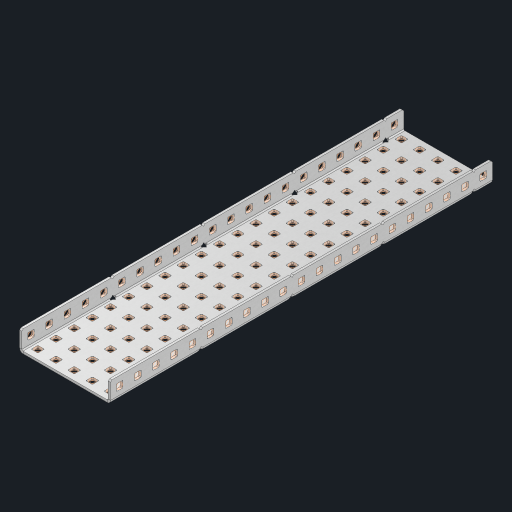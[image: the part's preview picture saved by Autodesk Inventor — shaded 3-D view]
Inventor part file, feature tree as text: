
AUTODESK INVENTOR PART (.ipt)
format: ipt  version: 2023 (Build 270158000, 158)  size: 1,718,272 bytes
history: native  units: in
note: dims shown in document units (in); Inventor stores cm internally (conversion verified against a paired STEP export)
features: other x152, extrude x146, sheet_metal_op x10, sketch x8, mirror x1, pattern_linear x1, chamfer x1
ambient origin geometry x8: Origin, YZ Plane, XZ Plane, XY Plane, X Axis, Y Axis, Z Axis, Center Point
bodies: Solid1 (feature_tree), Body (feature_tree)
feature tree (319):
  other  "Flange Pattern Plane"
  sheet_metal_op  "Flange Pattern"
  sheet_metal_op  "Body Pattern"
  other  "Arc Length"
  mirror  "Notch Mirror"
  pattern_linear  "Notch Pattern"  Spacing1=0.25in  [1 undecoded]
  chamfer  "End Chamfer"
  extrude  "Half Cut"  Depth=0.0625in
  sketch  "Sketch1"  dims[d0=2.5in]
  other  "Plate1"
  sketch  "Sketch2"  dims[d1=10.5in]
  other  "Plate2"
  sheet_metal_op  "Bend1"
  sheet_metal_op  "Corner1"
  sketch  "Sketch3"  dims[d2=0.0625in]
  other  "Flange Pattern Sketch"
  sketch  "Sketch7"  dims[d3=0.0625in]
  other  "Srf1"
  other  "Srf2"
  sketch  "Sketch8"  dims[d4=0.0312in]
  sketch  "Sketch9"  dims[d5=0.125in]
  other  "Srf91"
  sheet_metal_op  "Body Pattern Sketch"
  other  "Srf92"
  sketch  "Sketch13"  dims[d6=0.0625in]
  sketch  "Sketch14"  dims[d7=0.5in d8=90.0deg d9=0.0312in d10=0.25in d11=0.0625in d12=0.0625in d16=0.182in d17=0.02in d18=0.0625in d19=0.0in d20=0.25in d21=0.25in d46=0.172in d47=1.0in d48=0.0in d49=0.182in d50=0.02in d51=0.25in d52=0.25in d53=0.0625in d54=0.0in d55=0.172in d56=1.0in d57=0.0in d60=8.2677in d62=0.5in d63=1.9685in d65=0.5in d85=0.1473in d86=0.1782in d88=0.04in d89=0.0625in d90=0.0in d91=0.04in d92=0.0491in d95=2.5in d96=0.04in d97=0.25in d98=45.0deg d101=0.0in d102=2.497in d131=2.5in d132=8.2677in d134=0.5in d139=0.5in]
  other  "Srf856"
  other  "Srf1310"
  other  "Srf1311"
  other  "Srf1312"
  other  "Srf1376"
  other  "Srf1377"
  other  "Srf1728"
  other  "Srf1755"
  other  "Srf1878"
  other  "Srf1879"
  other  "Srf1880"
  other  "Srf1881"
  other  "Srf1882"
  other  "Srf1883"
  other  "Srf1884"
  other  "Srf1885"
  other  "Srf1886"
  other  "Srf1887"
  other  "Srf1888"
  other  "Srf1889"
  other  "Srf1890"
  other  "Srf1891"
  other  "Srf1892"
  other  "Srf1893"
  other  "Srf1894"
  other  "Srf1895"
  other  "Srf1896"
  other  "Srf1897"
  other  "Srf1898"
  other  "Srf1899"
  other  "Srf1900"
  other  "Srf1901"
  other  "Srf1902"
  other  "Srf1903"
  other  "Srf1904"
  other  "Srf1905"
  other  "Srf1906"
  other  "Srf1942"
  other  "Srf1943"
  other  "Srf1944"
  other  "Srf1945"
  other  "Srf1946"
  other  "Srf1947"
  other  "Srf1948"
  other  "Srf1949"
  other  "Srf1950"
  other  "Srf1951"
  other  "Srf1952"
  other  "Srf1953"
  other  "Srf1954"
  other  "Srf1955"
  other  "Srf1956"
  other  "Srf1957"
  other  "Srf1958"
  other  "Srf1959"
  other  "Srf1960"
  other  "Srf1961"
  other  "Srf1962"
  other  "Srf1963"
  other  "Srf1964"
  other  "Srf1965"
  other  "Srf1966"
  other  "Srf1967"
  other  "Srf1968"
  other  "Srf1969"
  other  "Srf1970"
  other  "Srf2111"
  other  "Srf2112"
  other  "Srf2113"
  other  "Srf2114"
  other  "Srf2115"
  other  "Srf2116"
  other  "Srf2117"
  other  "Srf2146"
  other  "Srf2147"
  other  "Srf2148"
  other  "Srf2149"
  other  "Srf2150"
  other  "Srf2151"
  other  "Srf2152"
  other  "Srf2153"
  other  "Srf2154"
  other  "Srf2155"
  other  "Srf2156"
  other  "Srf2157"
  other  "Srf2158"
  other  "Srf2159"
  other  "Srf2160"
  other  "Srf2161"
  other  "Srf2162"
  other  "Srf2163"
  other  "Srf2164"
  other  "Srf2165"
  other  "Srf2166"
  other  "Srf2167"
  other  "Srf2168"
  other  "Srf2169"
  other  "Srf2170"
  other  "Srf2171"
  other  "Srf2172"
  other  "Srf2173"
  other  "Srf2174"
  other  "Srf2175"
  other  "Srf2176"
  other  "Srf2177"
  other  "Srf2178"
  other  "Srf2179"
  other  "Srf2180"
  other  "Srf2181"
  other  "Srf2182"
  other  "Srf2183"
  other  "Srf2184"
  other  "Srf2185"
  other  "Srf2186"
  other  "Srf2187"
  other  "Srf2188"
  other  "Srf2189"
  other  "Srf2190"
  other  "Srf2191"
  other  "Srf2192"
  other  "Srf2193"
  other  "Srf2194"
  other  "Srf2195"
  other  "Srf2196"
  other  "Srf2197"
  other  "Srf2198"
  other  "Srf2199"
  other  "Srf2200"
  other  "Srf2201"
  other  "Srf2202"
  other  "Srf2203"
  other  "Srf2204"
  other  "Srf2205"
  other  "Srf2206"
  other  "Srf2207"
  other  "Srf2208"
  other  "Srf2209"
  other  "Srf2210"
  other  "Srf2211"
  other  "Srf2212"
  other  "Srf2213"
  other  "Srf2214"
  other  "Srf2215"
  sheet_metal_op  "Flange Stamp"
  sheet_metal_op  "Flange Circle"
  sheet_metal_op  "Body Stamp"
  sheet_metal_op  "Body Circle"
  sheet_metal_op  "Notch"
  extrude  "ExtrusionSrf2"  Depth=0.0625in
  extrude  "ExtrusionSrf92"  Depth=2.5in
  extrude  "ExtrusionSrf856"  Depth=0.02in
  extrude  "ExtrusionSrf1310"  Depth=0.0625in
  extrude  "ExtrusionSrf1311"  TaperAngle=0.0deg  [1 undecoded]
  extrude  "ExtrusionSrf1312"  Depth=0.25in
  extrude  "ExtrusionSrf1376"  Depth=0.25in
  extrude  "ExtrusionSrf1377"  Depth=2.5in
  extrude  "ExtrusionSrf1728"  Depth=2.5in TaperAngle=0.0deg
  extrude  "ExtrusionSrf1755"  Depth=2.5in
  extrude  "ExtrusionSrf1878"  Depth=0.02in
  extrude  "ExtrusionSrf1879"  Depth=0.25in
  extrude  "ExtrusionSrf1880"  Depth=0.25in
  extrude  "ExtrusionSrf1881"  Depth=0.0625in
  extrude  "ExtrusionSrf1882"  TaperAngle=0.0deg  [1 undecoded]
  extrude  "ExtrusionSrf1883"  Depth=2.5in
  extrude  "ExtrusionSrf1884"  Depth=2.5in TaperAngle=0.0deg
  extrude  "ExtrusionSrf1885"  Depth=2.5in
  extrude  "ExtrusionSrf1886"  Depth=2.5in
  extrude  "ExtrusionSrf1887"  Depth=2.5in
  extrude  "ExtrusionSrf1888"  Depth=2.5in
  extrude  "ExtrusionSrf1889"  Depth=2.5in
  extrude  "ExtrusionSrf1890"  Depth=0.0625in
  extrude  "ExtrusionSrf1891"  TaperAngle=0.0deg  [1 undecoded]
  extrude  "ExtrusionSrf1892"  Depth=2.5in
  extrude  "ExtrusionSrf1893"  Depth=2.5in
  extrude  "ExtrusionSrf1894"  Depth=2.5in
  extrude  "ExtrusionSrf1895"  Depth=0.25in TaperAngle=45.0deg
  extrude  "ExtrusionSrf1896"  TaperAngle=0.0deg  [1 undecoded]
  extrude  "ExtrusionSrf1897"  Depth=2.5in
  extrude  "ExtrusionSrf1898"  Depth=2.5in
  extrude  "ExtrusionSrf1899"  Depth=2.5in
  extrude  "ExtrusionSrf1900"  Depth=2.5in
  extrude  "ExtrusionSrf1901"  Depth=2.5in
  extrude  "ExtrusionSrf1902"  [1 undecoded]
  extrude  "ExtrusionSrf1903"  [1 undecoded]
  extrude  "ExtrusionSrf1904"  [1 undecoded]
  extrude  "ExtrusionSrf1905"  [1 undecoded]
  extrude  "ExtrusionSrf1906"  [1 undecoded]
  extrude  "ExtrusionSrf1942"  [1 undecoded]
  extrude  "ExtrusionSrf1943"  [1 undecoded]
  extrude  "ExtrusionSrf1944"  [1 undecoded]
  extrude  "ExtrusionSrf1945"  [1 undecoded]
  extrude  "ExtrusionSrf1946"  [1 undecoded]
  extrude  "ExtrusionSrf1947"  [1 undecoded]
  extrude  "ExtrusionSrf1948"  [1 undecoded]
  extrude  "ExtrusionSrf1949"  [1 undecoded]
  extrude  "ExtrusionSrf1950"  [1 undecoded]
  extrude  "ExtrusionSrf1951"  [1 undecoded]
  extrude  "ExtrusionSrf1952"  [1 undecoded]
  extrude  "ExtrusionSrf1953"  [1 undecoded]
  extrude  "ExtrusionSrf1954"  [1 undecoded]
  extrude  "ExtrusionSrf1955"  [1 undecoded]
  extrude  "ExtrusionSrf1956"  [1 undecoded]
  extrude  "ExtrusionSrf1957"  [1 undecoded]
  extrude  "ExtrusionSrf1958"  [1 undecoded]
  extrude  "ExtrusionSrf1959"  [1 undecoded]
  extrude  "ExtrusionSrf1960"  [1 undecoded]
  extrude  "ExtrusionSrf1961"  [1 undecoded]
  extrude  "ExtrusionSrf1962"  [1 undecoded]
  extrude  "ExtrusionSrf1963"  [1 undecoded]
  extrude  "ExtrusionSrf1964"  [1 undecoded]
  extrude  "ExtrusionSrf1965"  [1 undecoded]
  extrude  "ExtrusionSrf1966"  [1 undecoded]
  extrude  "ExtrusionSrf1967"  [1 undecoded]
  extrude  "ExtrusionSrf1968"  [1 undecoded]
  extrude  "ExtrusionSrf1969"  [1 undecoded]
  extrude  "ExtrusionSrf1970"  [1 undecoded]
  extrude  "ExtrusionSrf2111"  [1 undecoded]
  extrude  "ExtrusionSrf2112"  [1 undecoded]
  extrude  "ExtrusionSrf2113"  [1 undecoded]
  extrude  "ExtrusionSrf2114"  [1 undecoded]
  extrude  "ExtrusionSrf2115"  [1 undecoded]
  extrude  "ExtrusionSrf2116"  [1 undecoded]
  extrude  "ExtrusionSrf2117"  [1 undecoded]
  extrude  "ExtrusionSrf2146"  [1 undecoded]
  extrude  "ExtrusionSrf2147"  [1 undecoded]
  extrude  "ExtrusionSrf2148"  [1 undecoded]
  extrude  "ExtrusionSrf2149"  [1 undecoded]
  extrude  "ExtrusionSrf2150"  [1 undecoded]
  extrude  "ExtrusionSrf2151"  [1 undecoded]
  extrude  "ExtrusionSrf2152"  [1 undecoded]
  extrude  "ExtrusionSrf2153"  [1 undecoded]
  extrude  "ExtrusionSrf2154"  [1 undecoded]
  extrude  "ExtrusionSrf2155"  [1 undecoded]
  extrude  "ExtrusionSrf2156"  [1 undecoded]
  extrude  "ExtrusionSrf2157"  [1 undecoded]
  extrude  "ExtrusionSrf2158"  [1 undecoded]
  extrude  "ExtrusionSrf2159"  [1 undecoded]
  extrude  "ExtrusionSrf2160"  [1 undecoded]
  extrude  "ExtrusionSrf2161"  [1 undecoded]
  extrude  "ExtrusionSrf2162"  [1 undecoded]
  extrude  "ExtrusionSrf2163"  [1 undecoded]
  extrude  "ExtrusionSrf2164"  [1 undecoded]
  extrude  "ExtrusionSrf2165"  [1 undecoded]
  extrude  "ExtrusionSrf2166"  [1 undecoded]
  extrude  "ExtrusionSrf2167"  [1 undecoded]
  extrude  "ExtrusionSrf2168"  [1 undecoded]
  extrude  "ExtrusionSrf2169"  [1 undecoded]
  extrude  "ExtrusionSrf2170"  [1 undecoded]
  extrude  "ExtrusionSrf2171"  [1 undecoded]
  extrude  "ExtrusionSrf2172"  [1 undecoded]
  extrude  "ExtrusionSrf2173"  [1 undecoded]
  extrude  "ExtrusionSrf2174"  [1 undecoded]
  extrude  "ExtrusionSrf2175"  [1 undecoded]
  extrude  "ExtrusionSrf2176"  [1 undecoded]
  extrude  "ExtrusionSrf2177"  [1 undecoded]
  extrude  "ExtrusionSrf2178"  [1 undecoded]
  extrude  "ExtrusionSrf2179"  [1 undecoded]
  extrude  "ExtrusionSrf2180"  [1 undecoded]
  extrude  "ExtrusionSrf2181"  [1 undecoded]
  extrude  "ExtrusionSrf2182"  [1 undecoded]
  extrude  "ExtrusionSrf2183"  [1 undecoded]
  extrude  "ExtrusionSrf2184"  [1 undecoded]
  extrude  "ExtrusionSrf2185"  [1 undecoded]
  extrude  "ExtrusionSrf2186"  [1 undecoded]
  extrude  "ExtrusionSrf2187"  [1 undecoded]
  extrude  "ExtrusionSrf2188"  [1 undecoded]
  extrude  "ExtrusionSrf2189"  [1 undecoded]
  extrude  "ExtrusionSrf2190"  [1 undecoded]
  extrude  "ExtrusionSrf2191"  [1 undecoded]
  extrude  "ExtrusionSrf2192"  [1 undecoded]
  extrude  "ExtrusionSrf2193"  [1 undecoded]
  extrude  "ExtrusionSrf2194"  [1 undecoded]
  extrude  "ExtrusionSrf2195"  [1 undecoded]
  extrude  "ExtrusionSrf2196"  [1 undecoded]
  extrude  "ExtrusionSrf2197"  [1 undecoded]
  extrude  "ExtrusionSrf2198"  [1 undecoded]
  extrude  "ExtrusionSrf2199"  [1 undecoded]
  extrude  "ExtrusionSrf2200"  [1 undecoded]
  extrude  "ExtrusionSrf2201"  [1 undecoded]
  extrude  "ExtrusionSrf2202"  [1 undecoded]
  extrude  "ExtrusionSrf2203"  [1 undecoded]
  extrude  "ExtrusionSrf2204"  [1 undecoded]
  extrude  "ExtrusionSrf2205"  [1 undecoded]
  extrude  "ExtrusionSrf2206"  [1 undecoded]
  extrude  "ExtrusionSrf2207"  [1 undecoded]
  extrude  "ExtrusionSrf2208"  [1 undecoded]
  extrude  "ExtrusionSrf2209"  [1 undecoded]
  extrude  "ExtrusionSrf2210"  [1 undecoded]
  extrude  "ExtrusionSrf2211"  [1 undecoded]
  extrude  "ExtrusionSrf2212"  [1 undecoded]
  extrude  "ExtrusionSrf2213"  [1 undecoded]
  extrude  "ExtrusionSrf2214"  [1 undecoded]
  extrude  "ExtrusionSrf2215"  [1 undecoded]
note: 116 required parameter values undecoded (feature->parameter linkage not recoverable at this tier; creation-order binding heuristic only, values carry confidence <= 0.55)
